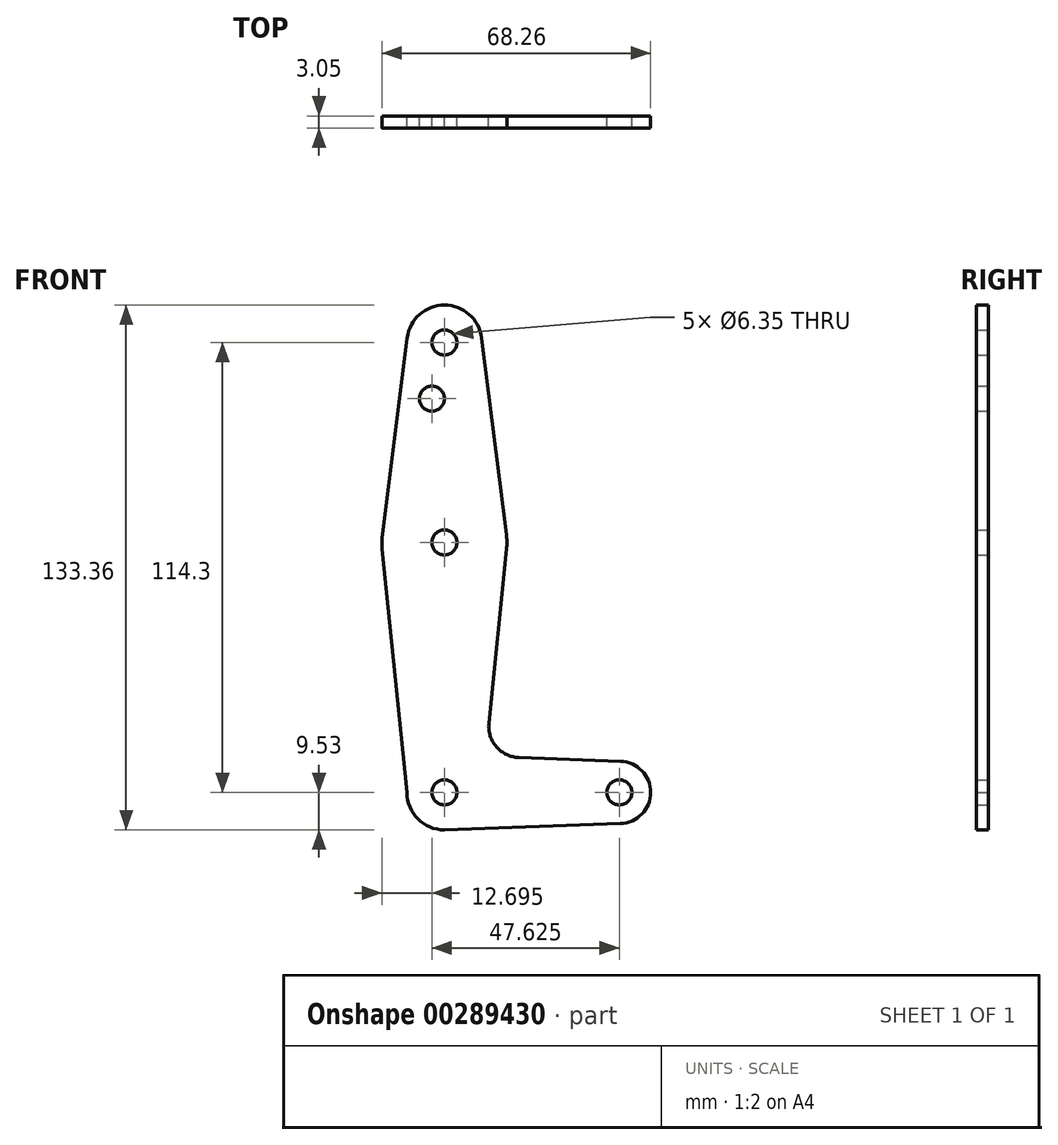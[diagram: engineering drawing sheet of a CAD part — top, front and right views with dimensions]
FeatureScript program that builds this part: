
annotation { "Feature Type Name" : "Feature", "Feature Type Description" : "" }
export const myFeature = defineFeature(function(context is Context, id is Id, definition is map)
    precondition{}
    {
        {
            var Q0;
            Q0=qCreatedBy(makeId("Front.planeOp"),FACE);
            var sketch = newSketch(context, id + "F0", { "sketchPlane" : qUnion([Q0])});
            skLineSegment(sketch, "E0", {"start": v(0, 114.3) * mm, "end": v(0, 0) * mm, "construction": true});
            skLineSegment(sketch, "E1", {"start": v(0, 0) * mm, "end": v(44.45, 0) * mm, "construction": true});
            skCircle(sketch, "E2", {"center": v(0, 114.3) * mm, "radius": 9.53 * mm});
            skCircle(sketch, "E3", {"center": v(0, 0) * mm, "radius": 9.53 * mm});
            skCircle(sketch, "E4", {"center": v(44.45, 0) * mm, "radius": 7.94 * mm});
            skCircle(sketch, "E5", {"center": v(0, 63.5) * mm, "radius": 15.88 * mm});
            skLineSegment(sketch, "E6", {"start": v(0, -9.53) * mm, "end": v(44.73, -7.93) * mm});
            skLineSegment(sketch, "E7", {"start": v(18.93, 8.85) * mm, "end": v(44.73, 7.93) * mm});
            skLineSegment(sketch, "E8", {"start": v(-9.45, 115.5) * mm, "end": v(-15.75, 65.48) * mm});
            skLineSegment(sketch, "E9", {"start": v(9.45, 115.5) * mm, "end": v(15.75, 65.48) * mm});
            skLineSegment(sketch, "E10", {"start": v(-9.53, 0) * mm, "end": v(-15.8, 61.9) * mm});
            skLineSegment(sketch, "E11", {"start": v(11.3, 17.6) * mm, "end": v(15.8, 61.9) * mm});
            skCircle(sketch, "E12", {"center": v(0, 114.3) * mm, "radius": 3.18 * mm});
            skCircle(sketch, "E13", {"center": v(-3.17, 100.03) * mm, "radius": 3.18 * mm});
            skCircle(sketch, "E14", {"center": v(0, 63.5) * mm, "radius": 3.18 * mm});
            skCircle(sketch, "E15", {"center": v(0, 0) * mm, "radius": 3.18 * mm});
            skCircle(sketch, "E16", {"center": v(44.45, 0) * mm, "radius": 3.18 * mm});
            skArc(sketch, "E17.filletArc", {"start": v(11.3, 17.6) * mm, "mid": v(13.22, 11.57) * mm, "end": v(18.93, 8.85) * mm});
            skSolve(sketch);
        }
        {
            var Q0;
            {var subQ1=sQuery(id+"F0.wireOp",EDGE,"E8");Q0=makeQuery(id+"F0.imprint","IMPRINT",FACE,{"disambiguationData":[TD([[makeQuery(id+"F0.imprint","IMPRINT",EDGE,{"derivedFrom":subQ1}),1.0]])]});}
            var Q1;
            Q1=makeQuery(id+"F0.imprint","IMPRINT",FACE,{"disambiguationData":[TD([[makeQuery(id+"F0.imprint","IMPRINT",EDGE,{"derivedFrom":sQuery(id+"F0.wireOp",EDGE,"E12")}),-1.0]])]});
            var Q2;
            Q2=makeQuery(id+"F0.imprint","IMPRINT",FACE,{"disambiguationData":[TD([[makeQuery(id+"F0.imprint","IMPRINT",EDGE,{"derivedFrom":sQuery(id+"F0.wireOp",EDGE,"E14")}),-1.0]])]});
            var Q3;
            {var subQ5=sQuery(id+"F0.wireOp",EDGE,"E7");Q3=makeQuery(id+"F0.imprint","IMPRINT",FACE,{"disambiguationData":[TD([[makeQuery(id+"F0.imprint","IMPRINT",EDGE,{"derivedFrom":subQ5}),-1.0]])]});}
            var Q4;
            Q4=makeQuery(id+"F0.imprint","IMPRINT",FACE,{"disambiguationData":[TD([[makeQuery(id+"F0.imprint","IMPRINT",EDGE,{"derivedFrom":sQuery(id+"F0.wireOp",EDGE,"E15")}),-1.0]])]});
            var Q5;
            Q5=makeQuery(id+"F0.imprint","IMPRINT",FACE,{"disambiguationData":[TD([[makeQuery(id+"F0.imprint","IMPRINT",EDGE,{"derivedFrom":sQuery(id+"F0.wireOp",EDGE,"E16")}),-1.0]])]});
            extrude(context, id + "F1", {"entities" : qUnion([Q0, Q1, Q2, Q3, Q4, Q5]), "depth" : 3.05 * mm});
        }
    });
